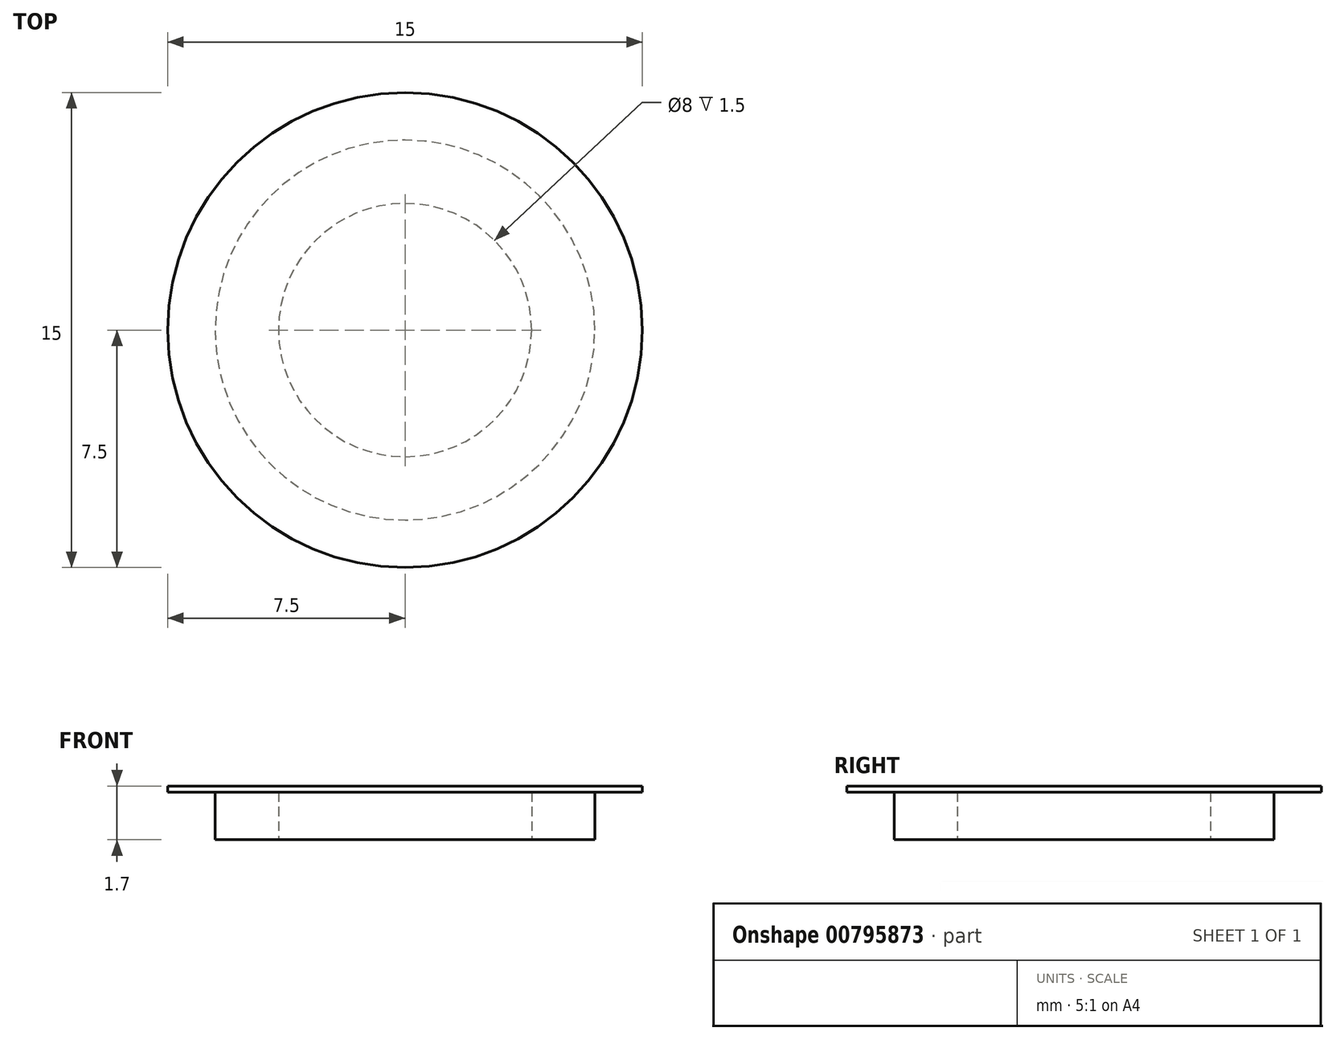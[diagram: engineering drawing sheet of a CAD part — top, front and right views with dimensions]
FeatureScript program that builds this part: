
annotation { "Feature Type Name" : "Feature", "Feature Type Description" : "" }
export const myFeature = defineFeature(function(context is Context, id is Id, definition is map)
    precondition{}
    {
        {
            var Q0;
            Q0=qCreatedBy(makeId("Front.planeOp"),FACE);
            var sketch = newSketch(context, id + "F0", { "sketchPlane" : qUnion([Q0])});
            skLineSegment(sketch, "E0", {"start": v(0, -2) * mm, "end": v(0, 8.65) * mm, "construction": true});
            skLineSegment(sketch, "E1.bottom", {"start": v(6, 0) * mm, "end": v(4, 0) * mm});
            skLineSegment(sketch, "E1.left", {"start": v(6, 0) * mm, "end": v(6, 1.5) * mm});
            skLineSegment(sketch, "E1.right", {"start": v(4, 0) * mm, "end": v(4, 1.5) * mm});
            skLineSegment(sketch, "E2", {"start": v(4, 1.5) * mm, "end": v(0, 1.5) * mm});
            skLineSegment(sketch, "E3.bottom", {"start": v(0, 1.7) * mm, "end": v(7.5, 1.7) * mm});
            skLineSegment(sketch, "E3.top", {"start": v(0, 1.5) * mm, "end": v(4, 1.5) * mm});
            skLineSegment(sketch, "E3.left", {"start": v(0, 1.7) * mm, "end": v(0, 1.5) * mm});
            skLineSegment(sketch, "E3.right", {"start": v(7.5, 1.7) * mm, "end": v(7.5, 1.5) * mm});
            skLineSegment(sketch, "E4.trimOffspring", {"start": v(6, 1.5) * mm, "end": v(7.5, 1.5) * mm});
            skSolve(sketch);
        }
        {
            var Q0;
            Q0 = qSketchRegion(id + "F0", true);
            var Q1;
            Q1=sQuery(id+"F0.wireOp",EDGE,"E0");
            revolve(context, id + "F1", {"surfaceOperationType" : NewSurfaceOperationType.NEW, "entities" : qUnion([Q0]), "axis" : qUnion([Q1]), "revolveType" : RevolveType.FULL});
        }
    });
